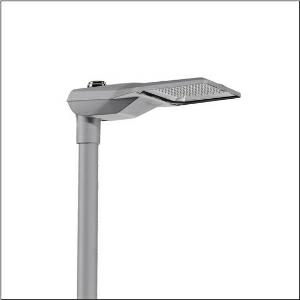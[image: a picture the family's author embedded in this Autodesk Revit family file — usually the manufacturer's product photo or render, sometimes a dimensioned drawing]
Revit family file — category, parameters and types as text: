
# Revit family: streetlight_sl_21_midi___stw1_0a_5xe7e47n08mb_f37a
name_source: partatom
category: Lighting Fixtures
units: mm (PartAtom-declared; Revit-internal decimal feet)

## family parameters
Cut with Voids When Loaded = No
Host = Face
Light Source = No
Part Type = Normal
Room Calculation Point = No
Round Connector Dimension = Use Diameter
Shared = No

## types (1)
- --- (1 x LED, 20180 lm, 147 W, 4000K)
    Apparent Load = 147 VA
    CIE Flux Codes = 38 75 98 100 100
    Color Rendering = 70
    Color Temperature = 4000K
    Default Elevation = 1800 mm
    Description = Streetlight SL 21 midi, mast luminaire, primary light control with lens, of PMMA, primary optical cover: cover, of toughened safety glass, transparent, light distribution: STW1.0a, light emission: direct distribution, primary light characteristic: asymmetric, installation type: side-entry, LED, 3G 2.5mm², High Power LED, rated luminous flux: 20.180lm, luminous efficacy: 137lm/W, light colour: 740, colour temperature: 4000K, control gear: NEMA (7pin), control: overheat protection, pre-setting: linear dimming characteristic, constant luminous flux control, time-dependent luminous flux control, flexible luminous flux parameterisation, mains connection: 220..240V, AC, 50/60Hz, connection cable pre-assembled, cable length: 12,5m, wiring characteristics: H05VV-F, start of lifetime: 147W, end of service life: 155W, reduction: 65W, luminaire housing, of diecast aluminium (EN AC-44300), powder-coated, SITECO metallic grey (DB 702S), corrosivity category C5 high according to DIN EN ISO 12944, multi-level sealing system, sealing non-destructively replaceable, inclination adjustable: 0°, 5°, 10°, 15°, length: 644mm, width: 335mm, height: 110mm, spigot size: 42mm (side-entry), mounting height: 4..8m, protection rating (complete): IP66, insulation class (complete): insulation class I (protective earthing), certification: CE, ENEC, ENEC+, VDE, impact resistance: IK10, permissible operating ambient temperature for outdoor applications: -40..+50°C, standard-compliant lighting for roads and squares, packaging unit: 1 piece

Light Distribution: STW1.0a
    Height = 111 mm
    Lamp = 1 x LED
    Lamp Light Flux = 20180 lm
    Lamp Power = 147 W
    Lamp count = 1
    Length = 644 mm
    Luminous efficacy = 137 lm/W
    Manufacturer = Siteco
    ModVariant = No
    Model = 5XE7E47N08MB
    Number of Poles = 1
    OnlyDefault = Yes
    Power Factor = 1
    Product Name = Streetlight SL 21 midi | STW1.0a
    Product group = mast luminaire | pylon top
    ProductGroupID = 6100
    Protection Class = Protection class I
    Protection Degree = IP 66
    RLX_Detail_Level = 1
    RLX_Emergency_Light_Flux = 0 lm
    RLX_Emergency_Type = 0
    RLX_Emergency_Type_DB = No
    RlxData = <blob elided: 26609 chars, md5=64d6dc8e>
    Socket = socket
    Standby Power = 0 W
    System Light Flux = 20180 lm
    System Power = 147 W
    Type Comments = factory setting: luminous flux: 100 % | dim-lin: 254 | 750 mA
    Type Image = l_1294377.jpg
    URL = http://relux.com
    VarID = @adj_134937
    Voltage = 0 V
    Weight = 0.00 kg
    Width = 336 mm

## geometry (parser evidence)
native form markers: Blend x4, Sweep x10
no freeform markers — native parametric forms only
